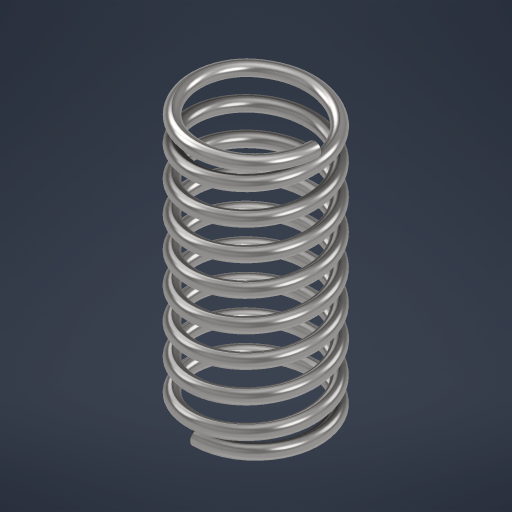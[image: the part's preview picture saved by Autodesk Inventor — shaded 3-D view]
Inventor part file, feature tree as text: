
AUTODESK INVENTOR PART (.ipt)
format: ipt  version: 2025 (Build 290162010, 162A)  size: 804,864 bytes
history: native  units: mm
features: helix x1
ambient origin geometry x8: Origin, YZ Plane, XZ Plane, XY Plane, X Axis, Y Axis, Z Axis, Center Point
bodies: Body1 (feature_tree)
feature tree (1):
  helix  "Coil2"  [1 undecoded]
note: 1 required parameter value undecoded (feature->parameter linkage not recoverable at this tier; creation-order binding heuristic only, values carry confidence <= 0.55)
